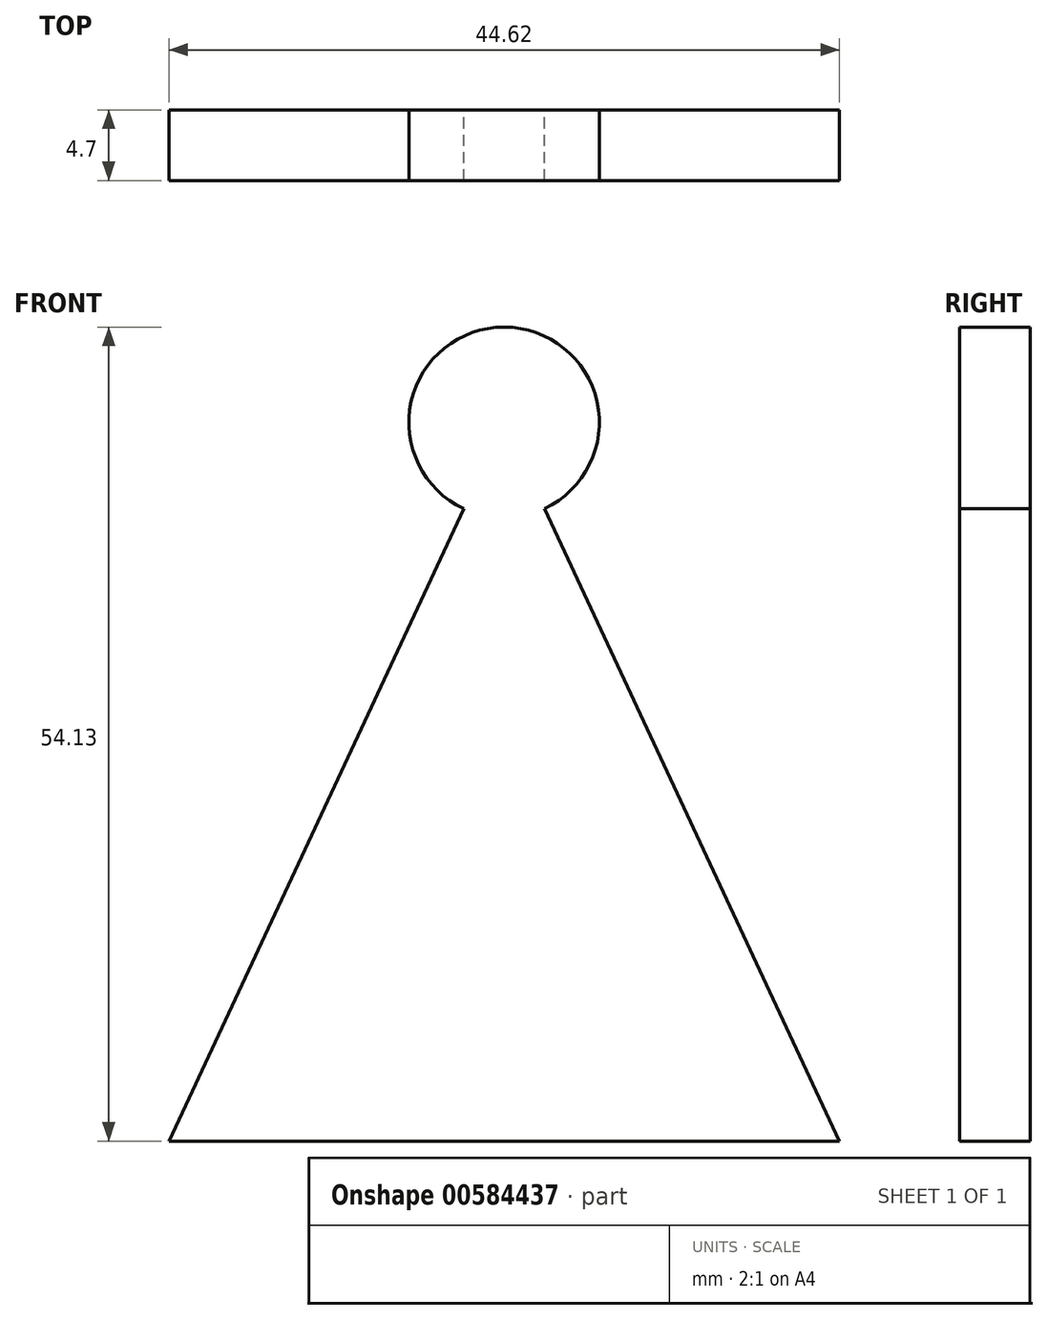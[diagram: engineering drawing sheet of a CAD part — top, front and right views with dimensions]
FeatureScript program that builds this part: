
annotation { "Feature Type Name" : "Feature", "Feature Type Description" : "" }
export const myFeature = defineFeature(function(context is Context, id is Id, definition is map)
    precondition{}
    {
        {
            var Q0;
            Q0=qCreatedBy(makeId("Front.planeOp"),FACE);
            var sketch = newSketch(context, id + "F0", { "sketchPlane" : qUnion([Q0])});
            skLineSegment(sketch, "E0", {"start": v(-67.4, 3.94) * mm, "end": v(-22.78, 3.94) * mm});
            skLineSegment(sketch, "E1", {"start": v(-67.4, 3.94) * mm, "end": v(-45.1, 51.73) * mm});
            skLineSegment(sketch, "E2", {"start": v(-45.1, 51.73) * mm, "end": v(-22.78, 3.94) * mm});
            skPoint(sketch, "E3.start.orphan", {"position": v(-67.4, 51.73) * mm});
            skPoint(sketch, "E4.start.orphan", {"position": v(-67.4, 27.92) * mm});
            skPoint(sketch, "E5.start.orphan", {"position": v(-22.78, 27.92) * mm});
            skCircle(sketch, "E6", {"center": v(-45.1, 51.73) * mm, "radius": 6.34 * mm});
            skSolve(sketch);
        }
        {
            var Q0;
            Q0 = qSketchRegion(id + "F0", true);
            extrude(context, id + "F1", {"entities" : qUnion([Q0]), "depth" : 4.7 * mm, "offsetDistance" : 25 * mm});
        }
    });
